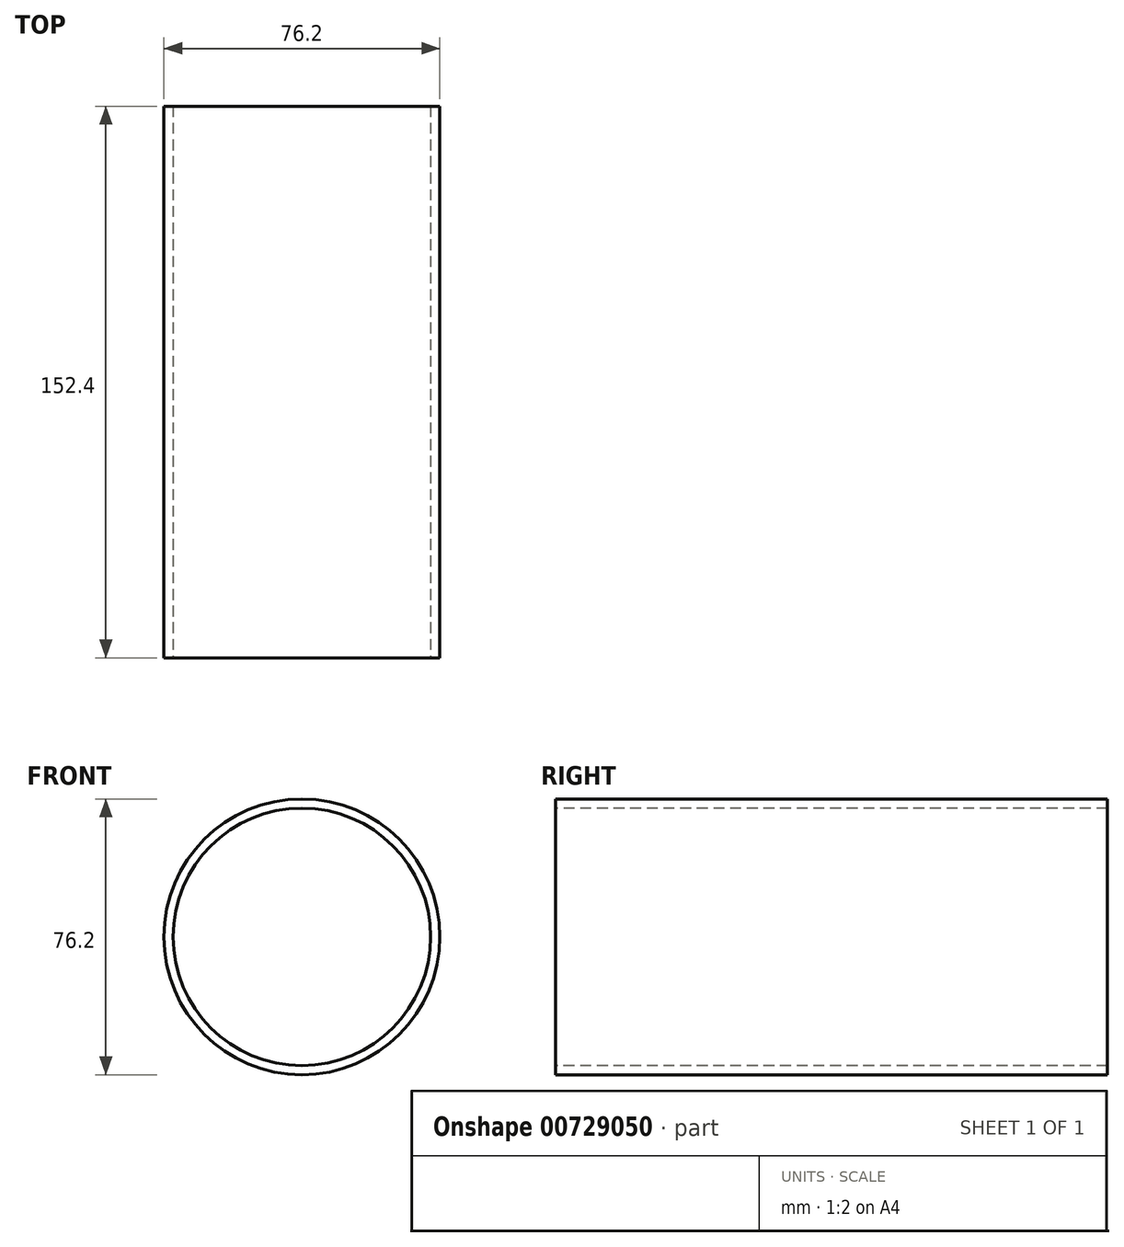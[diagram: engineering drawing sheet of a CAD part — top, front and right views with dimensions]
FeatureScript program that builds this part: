
annotation { "Feature Type Name" : "Feature", "Feature Type Description" : "" }
export const myFeature = defineFeature(function(context is Context, id is Id, definition is map)
    precondition{}
    {
        {
            var Q0;
            Q0=qCreatedBy(makeId("Front.planeOp"),FACE);
            var sketch = newSketch(context, id + "F0", { "sketchPlane" : qUnion([Q0])});
            skCircle(sketch, "E0", {"center": v(0, 0) * mm, "radius": 38.1 * mm});
            skSolve(sketch);
        }
        {
            var Q0;
            Q0 = qSketchRegion(id + "F0", true);
            extrude(context, id + "F1", {"entities" : qUnion([Q0]), "depth" : 152.4 * mm, "offsetDistance" : 25.4 * mm});
        }
        {
            var Q0;
            Q0=makeQuery(id+"F1.opExtrude","CAP_FACE",FACE,{"disambiguationData":[OSD([sQuery(id+"F0.wireOp",EDGE,"E0")])],"isStart":false});
            var sketch = newSketch(context, id + "F2", { "sketchPlane" : qUnion([Q0])});
            skCircle(sketch, "E1", {"center": v(0, 0) * mm, "radius": 35.56 * mm});
            skSolve(sketch);
        }
        {
            var Q0;
            Q0 = qSketchRegion(id + "F2", true);
            extrude(context, id + "F3", {"entities" : qUnion([Q0]), "operationType" : NewBodyOperationType.REMOVE, "endBound" : BoundingType.THROUGH_ALL, "oppositeDirection" : true, "depth" : 25.4 * mm, "offsetDistance" : 25.4 * mm});
        }
    });
